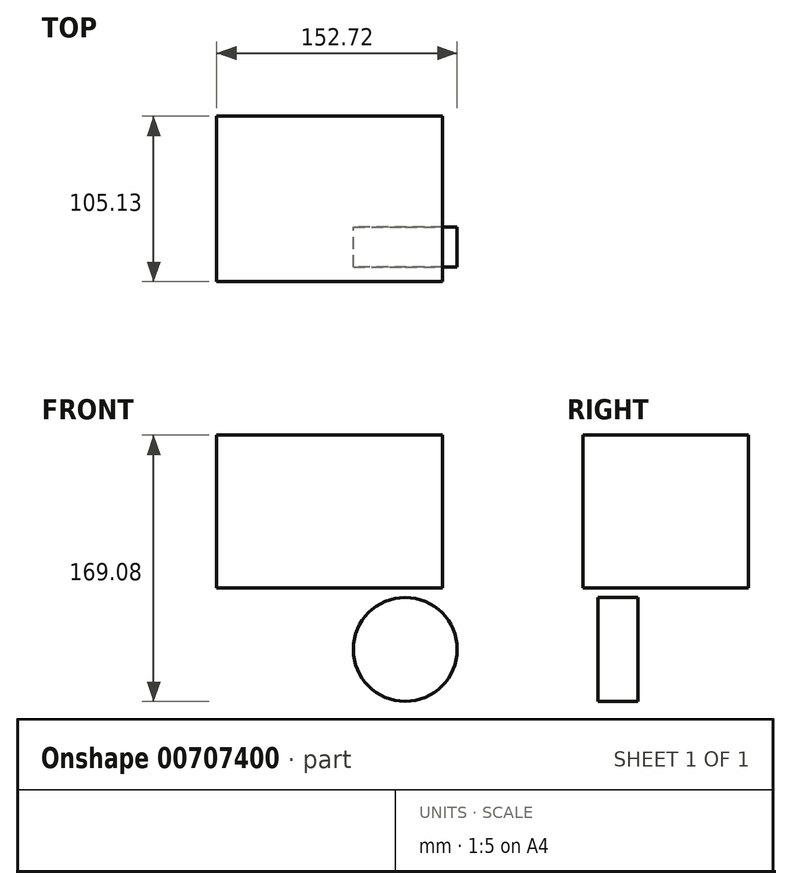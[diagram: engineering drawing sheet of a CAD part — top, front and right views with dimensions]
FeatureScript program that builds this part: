
annotation { "Feature Type Name" : "Feature", "Feature Type Description" : "" }
export const myFeature = defineFeature(function(context is Context, id is Id, definition is map)
    precondition{}
    {
        {
            var Q0;
            Q0=qCreatedBy(makeId("Top.planeOp"),FACE);
            var sketch = newSketch(context, id + "F0", { "sketchPlane" : qUnion([Q0])});
            skLineSegment(sketch, "E0.bottom", {"start": v(-107.1, 70.4) * mm, "end": v(36.37, 70.4) * mm});
            skLineSegment(sketch, "E0.top", {"start": v(-107.1, -34.73) * mm, "end": v(36.37, -34.73) * mm});
            skLineSegment(sketch, "E0.left", {"start": v(-107.1, 70.4) * mm, "end": v(-107.1, -34.73) * mm});
            skLineSegment(sketch, "E0.right", {"start": v(36.37, 70.4) * mm, "end": v(36.37, -34.73) * mm});
            skSolve(sketch);
        }
        {
            var Q0;
            Q0 = qSketchRegion(id + "F0", true);
            extrude(context, id + "F1", {"entities" : qUnion([Q0]), "depth" : 97.03 * mm, "offsetDistance" : 25.4 * mm});
        }
        {
            var Q0;
            Q0=qCreatedBy(makeId("Front.planeOp"), FACE);
            var sketch = newSketch(context, id + "F2", { "sketchPlane" : qUnion([Q0])});
            skCircle(sketch, "E1", {"center": v(12.63, -39.05) * mm, "radius": 33 * mm});
            skSolve(sketch);
        }
        {
            var Q0;
            Q0 = qSketchRegion(id + "F2", true);
            extrude(context, id + "F3", {"entities" : qUnion([Q0]), "domain" : OperationDomain.MODEL, "flatOperationType" : FlatOperationType.REMOVE, "depth" : 25.4 * mm, "offsetDistance" : 25.4 * mm});
        }
    });
